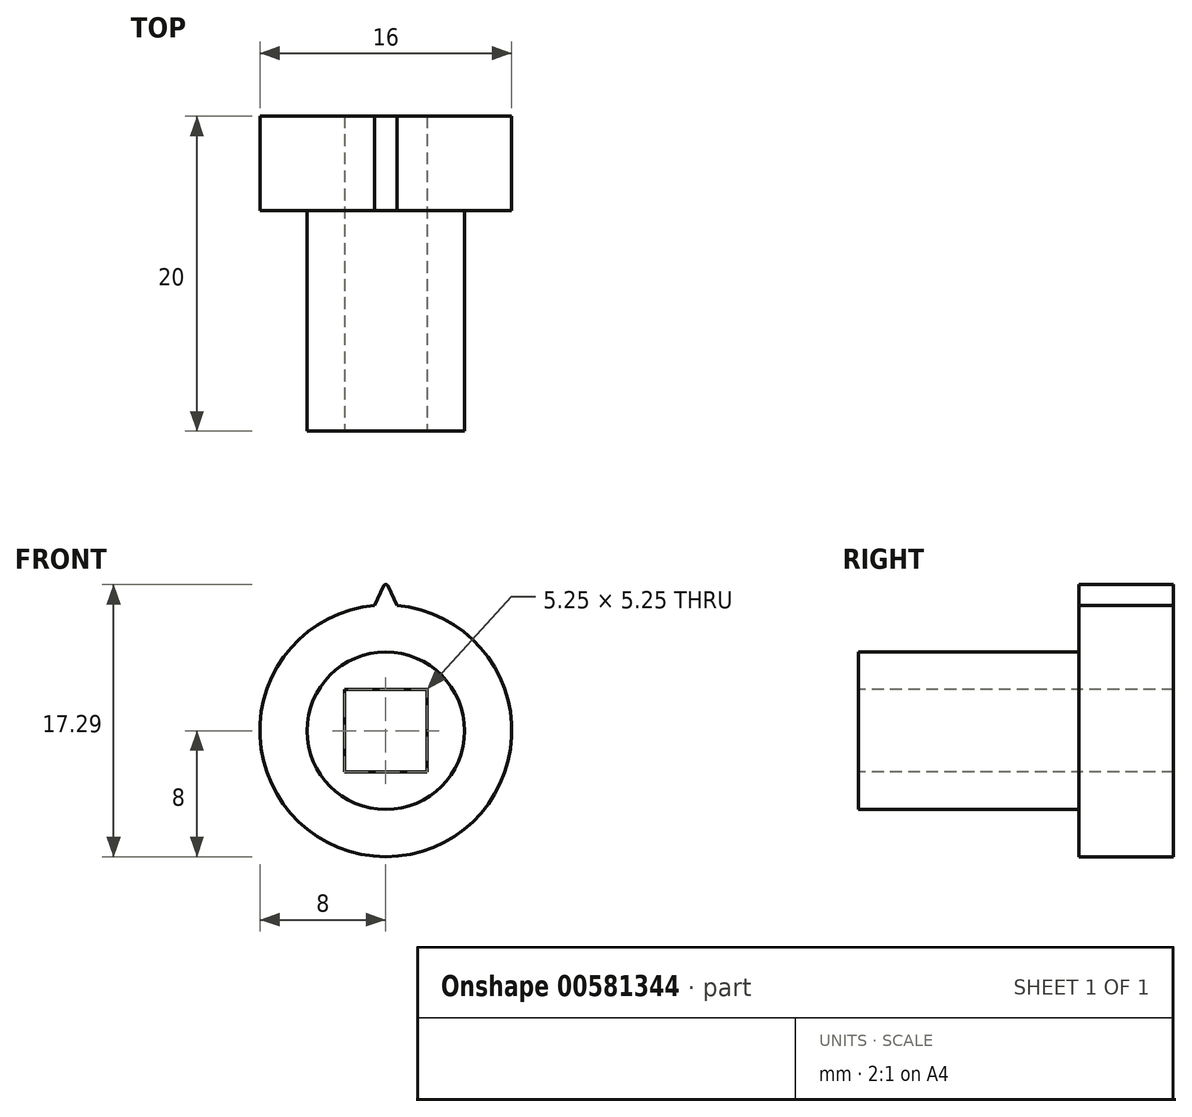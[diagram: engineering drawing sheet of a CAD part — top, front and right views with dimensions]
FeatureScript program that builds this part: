
annotation { "Feature Type Name" : "Feature", "Feature Type Description" : "" }
export const myFeature = defineFeature(function(context is Context, id is Id, definition is map)
    precondition{}
    {
        {
            var Q0;
            Q0=qCreatedBy(makeId("Front.planeOp"),FACE);
            var sketch = newSketch(context, id + "F0", { "sketchPlane" : qUnion([Q0])});
            skCircle(sketch, "E0", {"center": v(0, 0) * mm, "radius": 8 * mm});
            skCircle(sketch, "E1", {"center": v(0, 0) * mm, "radius": 5 * mm});
            skSolve(sketch);
        }
        {
            var Q0;
            Q0=makeQuery(id+"F0.imprint","IMPRINT",FACE,{"disambiguationData":[TD([[makeQuery(id+"F0.imprint","IMPRINT",EDGE,{"derivedFrom":sQuery(id+"F0.wireOp",EDGE,"E0")}),1.0]])]});
            var Q1;
            Q1=makeQuery(id+"F0.imprint","IMPRINT",FACE,{"disambiguationData":[TD([[makeQuery(id+"F0.imprint","IMPRINT",EDGE,{"derivedFrom":sQuery(id+"F0.wireOp",EDGE,"E1")}),1.0]])]});
            extrude(context, id + "F1", {"entities" : qUnion([Q0, Q1]), "depth" : 6 * mm, "offsetDistance" : 25 * mm});
        }
        {
            var Q0;
            Q0=makeQuery(id+"F0.imprint","IMPRINT",FACE,{"disambiguationData":[TD([[makeQuery(id+"F0.imprint","IMPRINT",EDGE,{"derivedFrom":sQuery(id+"F0.wireOp",EDGE,"E1")}),1.0]])]});
            extrude(context, id + "F2", {"entities" : qUnion([Q0]), "operationType" : NewBodyOperationType.ADD, "depth" : 20 * mm, "offsetDistance" : 25 * mm});
        }
        {
            var Q0;
            Q0=makeQuery(id+"F2.opExtrude","CAP_FACE",FACE,{"disambiguationData":[OSD([sQuery(id+"F0.wireOp",EDGE,"E1")])],"isStart":false});
            var sketch = newSketch(context, id + "F3", { "sketchPlane" : qUnion([Q0])});
            skLineSegment(sketch, "E2.bottom", {"start": v(2.63, -2.62) * mm, "end": v(-2.62, -2.63) * mm});
            skLineSegment(sketch, "E2.top", {"start": v(2.62, 2.63) * mm, "end": v(-2.63, 2.62) * mm});
            skLineSegment(sketch, "E2.left", {"start": v(2.63, -2.62) * mm, "end": v(2.62, 2.63) * mm});
            skLineSegment(sketch, "E2.right", {"start": v(-2.62, -2.63) * mm, "end": v(-2.63, 2.62) * mm});
            skPoint(sketch, "E2.middle", {"position": v(0, 0) * mm});
            skSolve(sketch);
        }
        {
            var Q0;
            Q0=makeQuery(id+"F3.imprint","IMPRINT",FACE,{"disambiguationData":[TD([[makeQuery(id+"F3.imprint","IMPRINT",EDGE,{"derivedFrom":sQuery(id+"F3.wireOp",EDGE,"E2.bottom")}),-1.0]])]});
            extrude(context, id + "F4", {"entities" : qUnion([Q0]), "operationType" : NewBodyOperationType.REMOVE, "oppositeDirection" : true, "depth" : 26 * mm, "offsetDistance" : 25 * mm});
        }
        {
            var Q0;
            Q0=makeQuery(id+"F1.opExtrude","CAP_FACE",FACE,{"disambiguationData":[OSD([sQuery(id+"F0.wireOp",EDGE,"E0")])],"isStart":true});
            var sketch = newSketch(context, id + "F5", { "sketchPlane" : qUnion([Q0])});
            skLineSegment(sketch, "E3", {"start": v(0, 8) * mm, "end": v(0, 9.5) * mm, "construction": true});
            skLineSegment(sketch, "E4", {"start": v(0, 8) * mm, "end": v(-0.7, 7.97) * mm});
            skLineSegment(sketch, "E5", {"start": v(-0.7, 7.97) * mm, "end": v(0, 9.5) * mm});
            skLineSegment(sketch, "E6", {"start": v(0, 8) * mm, "end": v(0.7, 7.97) * mm});
            skLineSegment(sketch, "E7", {"start": v(0.7, 7.97) * mm, "end": v(0, 9.5) * mm});
            skSolve(sketch);
        }
        {
            var Q0;
            {var subQ0=sQuery(id+"F5.wireOp",EDGE,"E5");Q0=makeQuery(id+"F5.imprint","IMPRINT",FACE,{"disambiguationData":[TD([[makeQuery(id+"F5.imprint","IMPRINT",EDGE,{"derivedFrom":subQ0}),-1.0]])]});}
            extrude(context, id + "F6", {"entities" : qUnion([Q0]), "operationType" : NewBodyOperationType.ADD, "depth" : -6 * mm, "offsetDistance" : 25 * mm});
        }
        {
            var Q0;
            Q0=makeQuery(id+"F6.opExtrude","SWEPT_EDGE",EDGE,{"disambiguationData":[OSD([sQuery(id+"F0.wireOp",EDGE,"E0"),sQuery(id+"F5.wireOp",EDGE,"E4"),sQuery(id+"F5.wireOp",EDGE,"E5")])]});
            var Q1;
            Q1=makeQuery(id+"F6.opExtrude","SWEPT_EDGE",EDGE,{"disambiguationData":[OSD([sQuery(id+"F0.wireOp",EDGE,"E0"),sQuery(id+"F5.wireOp",EDGE,"E6"),sQuery(id+"F5.wireOp",EDGE,"E7")])]});
            var Q2;
            Q2=makeQuery(id+"F6.opExtrude","SWEPT_EDGE",EDGE,{"disambiguationData":[OSD([sQuery(id+"F5.wireOp",EDGE,"E5"),sQuery(id+"F5.wireOp",EDGE,"E7")])]});
            fillet(context, id + "F7", {"entities" : qUnion([Q0, Q1, Q2]), "radius" : .15 * mm, "tangentPropagation" : true, "allowEdgeOverflow" : false});
        }
    });
